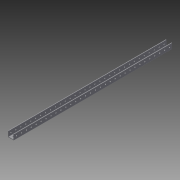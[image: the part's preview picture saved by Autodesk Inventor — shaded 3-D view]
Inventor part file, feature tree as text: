
AUTODESK INVENTOR PART (.ipt)
format: ipt  version: 2014 (Build 180170000, 170)  size: 184,832 bytes
history: native  units: in
note: dims shown in document units (in); Inventor stores cm internally (conversion verified against a paired STEP export)
features: sketch x3, hole x2, pattern_linear x2, extrude x1
ambient origin geometry x8: Origin, YZ Plane, XZ Plane, XY Plane, X Axis, Y Axis, Z Axis, Center Point
bodies: Solid1 (feature_tree)
feature tree (8):
  extrude  "Extrusion1"  Depth=1.125in
  hole  "Hole1"  [1 undecoded]
  pattern_linear  "Rectangular Pattern1"  Spacing1=0.5in  [1 undecoded]
  hole  "Hole2"  [1 undecoded]
  pattern_linear  "Rectangular Pattern2"  Spacing1=0.5in  [1 undecoded]
  sketch  "Sketch1"  dims[d0=1.25in d1=1.125in]
  sketch  "Sketch2"  dims[d4=0.0625in d5=0.125in]
  sketch  "Sketch3"  dims[d6=32.0in d7=0.0in d8=0.5in d9=0.25in d10=0.75in d11=0.375in d12=0.25in d13=0.5635in d14=1.0in d15=0.8108in d16=12.5984in d18=1.0in d19=0.5in d20=0.25in d21=0.75in d22=0.375in d23=0.25in d24=0.5635in d25=1.0in d26=0.8108in d27=12.5984in d29=1.0in]
note: 4 required parameter values undecoded (feature->parameter linkage not recoverable at this tier; creation-order binding heuristic only, values carry confidence <= 0.55)
